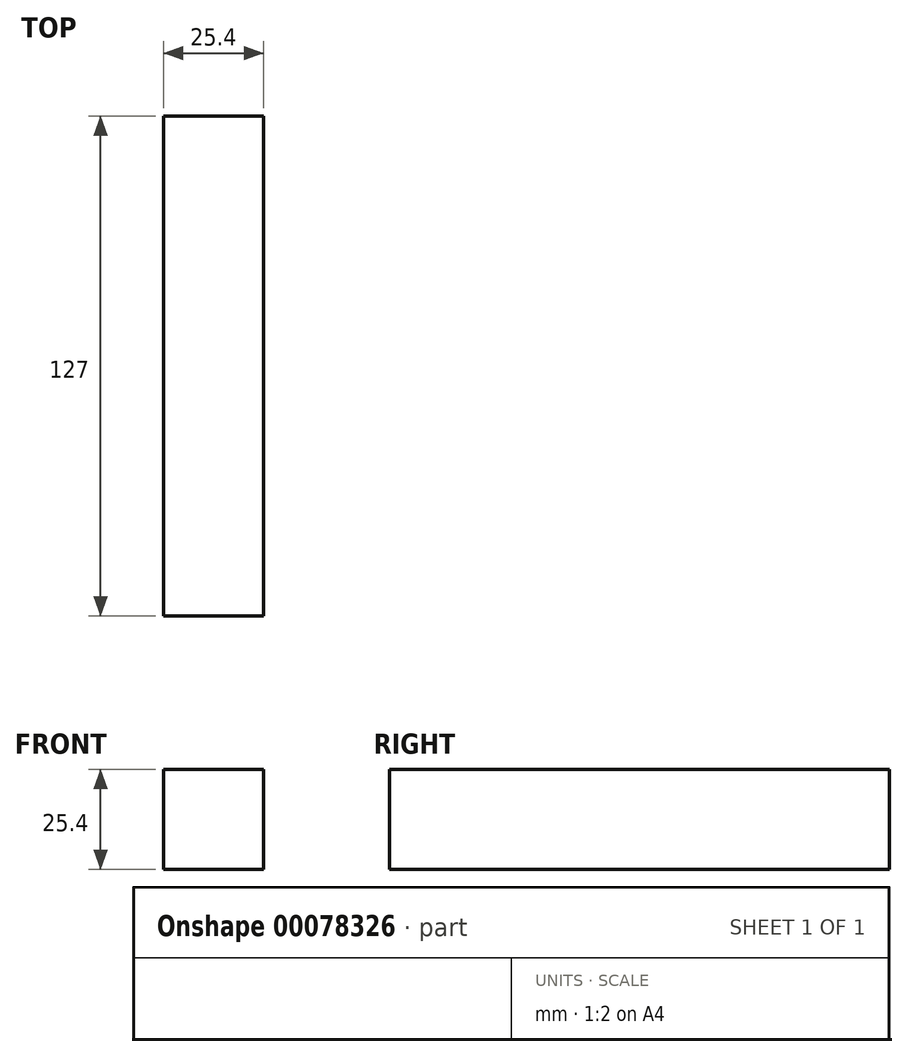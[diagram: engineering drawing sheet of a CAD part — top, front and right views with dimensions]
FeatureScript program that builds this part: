
annotation { "Feature Type Name" : "Feature", "Feature Type Description" : "" }
export const myFeature = defineFeature(function(context is Context, id is Id, definition is map)
    precondition{}
    {
        {
            var Q0;
            Q0=qCreatedBy(makeId("Front.planeOp"),FACE);
            var sketch = newSketch(context, id + "F0", { "sketchPlane" : qUnion([Q0])});
            skLineSegment(sketch, "E0", {"start": v(0, 0) * mm, "end": v(0, 25.4) * mm});
            skLineSegment(sketch, "E1", {"start": v(0, 25.4) * mm, "end": v(25.4, 25.4) * mm});
            skLineSegment(sketch, "E2", {"start": v(25.4, 25.4) * mm, "end": v(25.4, 0) * mm});
            skLineSegment(sketch, "E3", {"start": v(25.4, 0) * mm, "end": v(0, 0) * mm});
            skSolve(sketch);
        }
        {
            var Q0;
            Q0 = qSketchRegion(id + "F0", true);
            extrude(context, id + "F1", {"entities" : qUnion([Q0]), "depth" : 127 * mm});
        }
    });
